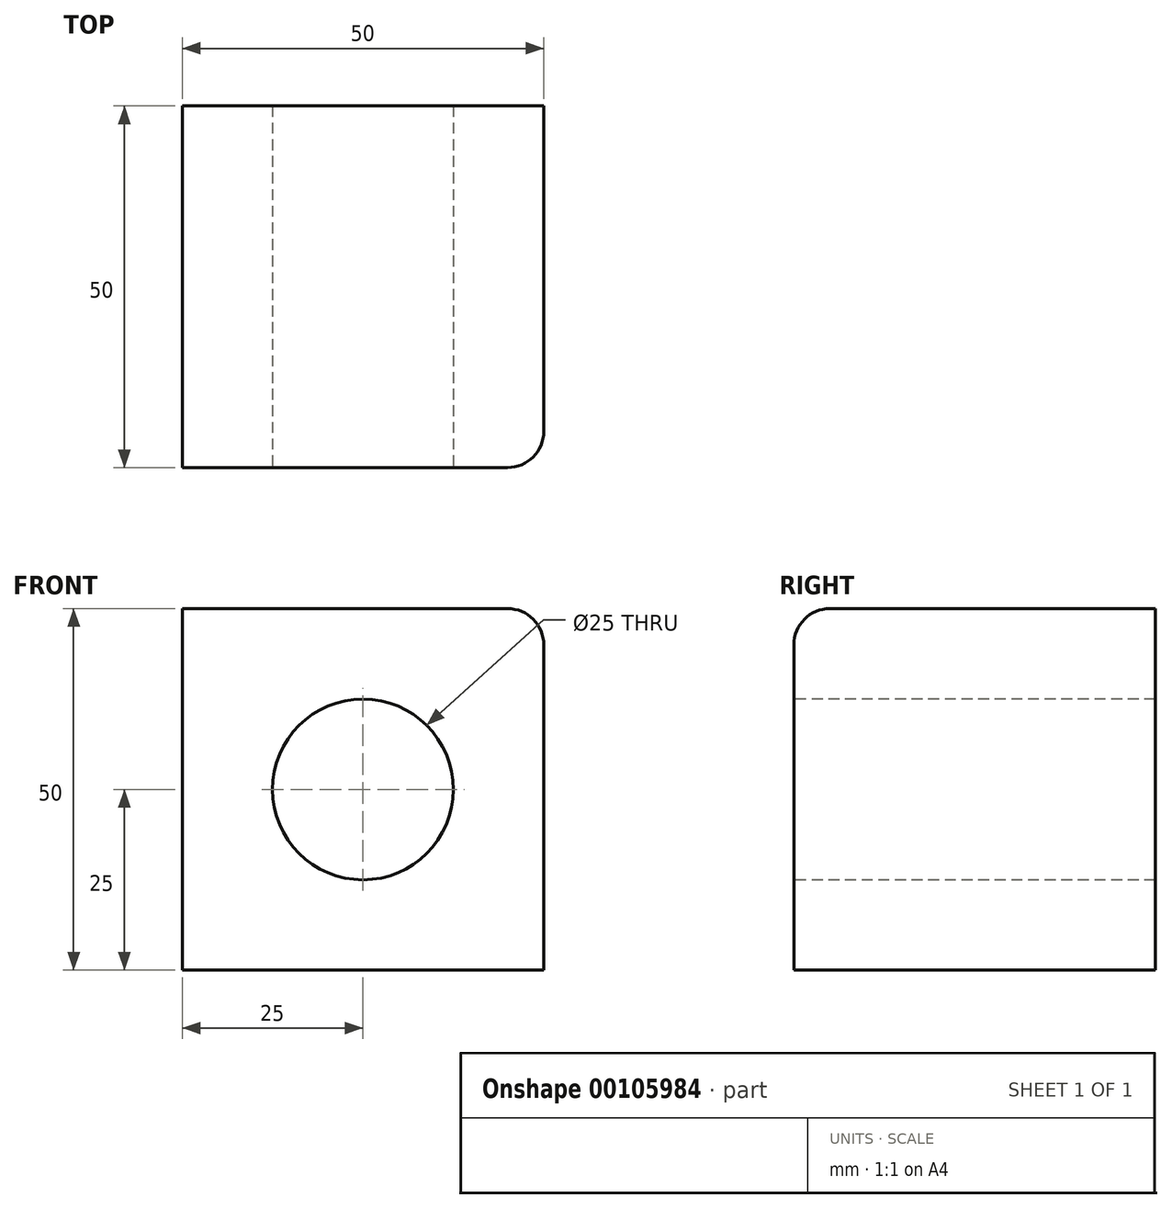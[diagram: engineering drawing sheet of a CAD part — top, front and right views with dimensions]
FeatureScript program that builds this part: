
annotation { "Feature Type Name" : "Feature", "Feature Type Description" : "" }
export const myFeature = defineFeature(function(context is Context, id is Id, definition is map)
    precondition{}
    {
        {
            var Q0;
            Q0=qCreatedBy(makeId("Top.planeOp"),FACE);
            var sketch = newSketch(context, id + "F0", { "sketchPlane" : qUnion([Q0])});
            skLineSegment(sketch, "E0.bottom", {"start": v(0, 0) * mm, "end": v(50, 0) * mm});
            skLineSegment(sketch, "E0.top", {"start": v(0, 50) * mm, "end": v(50, 50) * mm});
            skLineSegment(sketch, "E0.left", {"start": v(0, 0) * mm, "end": v(0, 50) * mm});
            skLineSegment(sketch, "E0.right", {"start": v(50, 0) * mm, "end": v(50, 50) * mm});
            skSolve(sketch);
        }
        {
            var Q0;
            Q0=makeQuery(id+"F0.imprint","IMPRINT",FACE,{"disambiguationData":[TD([[makeQuery(id+"F0.imprint","IMPRINT",EDGE,{"derivedFrom":sQuery(id+"F0.wireOp",EDGE,"E0.bottom")}),1.0]])]});
            extrude(context, id + "F1", {"entities" : qUnion([Q0]), "depth" : 50 * mm});
        }
        {
            var Q0;
            Q0=makeQuery(id+"F1.opExtrude","SWEPT_FACE",FACE,{"disambiguationData":[OSD([sQuery(id+"F0.wireOp",EDGE,"E0.bottom")])]});
            var sketch = newSketch(context, id + "F2", { "sketchPlane" : qUnion([Q0])});
            skCircle(sketch, "E1", {"center": v(25, 25) * mm, "radius": 12.5 * mm});
            skPoint(sketch, "E1.centerSnap0", {"position": v(50, 25) * mm});
            skPoint(sketch, "E1.centerSnap1", {"position": v(25, 50) * mm});
            skSolve(sketch);
        }
        {
            var Q0;
            Q0 = qSketchRegion(id + "F2", true);
            extrude(context, id + "F3", {"entities" : qUnion([Q0]), "operationType" : NewBodyOperationType.REMOVE, "endBound" : BoundingType.THROUGH_ALL, "oppositeDirection" : true, "depth" : 25 * mm});
        }
        {
            var Q0;
            Q0=makeQuery(id+"F1.opExtrude","CAP_EDGE",EDGE,{"disambiguationData":[OSD([sQuery(id+"F0.wireOp",EDGE,"E0.bottom")])],"isStart":false});
            var Q1;
            Q1=makeQuery(id+"F1.opExtrude","CAP_EDGE",EDGE,{"disambiguationData":[OSD([sQuery(id+"F0.wireOp",EDGE,"E0.right")])],"isStart":false});
            var Q2;
            Q2=makeQuery(id+"F1.opExtrude","SWEPT_EDGE",EDGE,{"disambiguationData":[OSD([sQuery(id+"F0.wireOp",EDGE,"E0.bottom"),sQuery(id+"F0.wireOp",EDGE,"E0.right")])]});
            fillet(context, id + "F4", {"entities" : qUnion([Q0, Q1, Q2]), "radius" : 5 * mm, "tangentPropagation" : true, "allowEdgeOverflow" : false});
        }
    });
